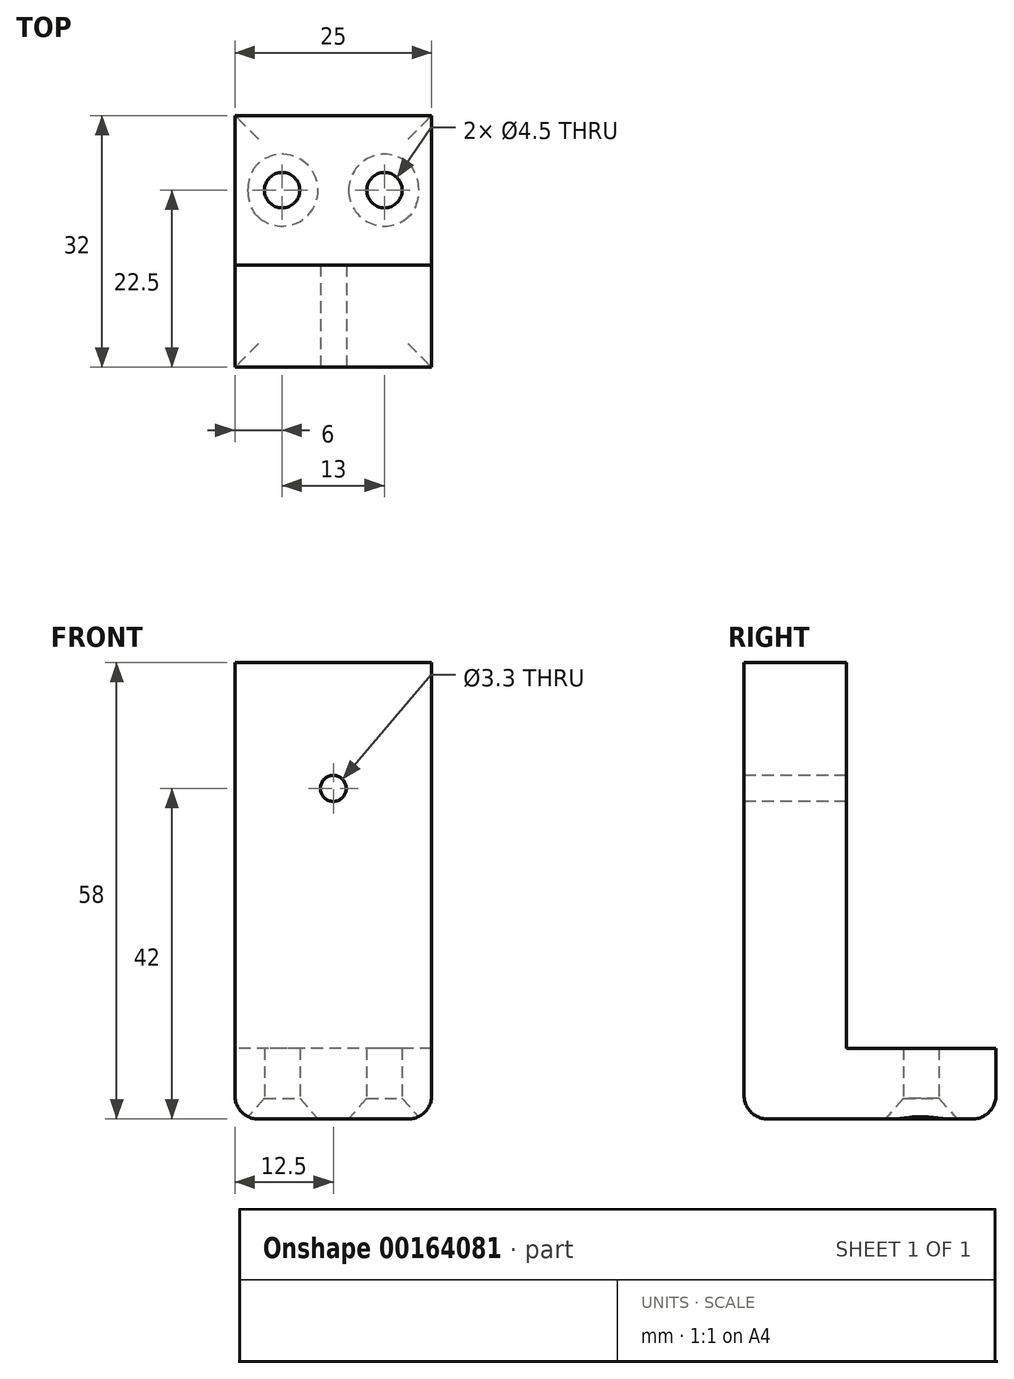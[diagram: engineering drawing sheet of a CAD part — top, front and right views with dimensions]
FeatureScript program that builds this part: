
annotation { "Feature Type Name" : "Feature", "Feature Type Description" : "" }
export const myFeature = defineFeature(function(context is Context, id is Id, definition is map)
    precondition{}
    {
        {
            var Q0;
            Q0=qCreatedBy(makeId("Right.planeOp"),FACE);
            var sketch = newSketch(context, id + "F0", { "sketchPlane" : qUnion([Q0])});
            skLineSegment(sketch, "E0", {"start": v(19, -58) * mm, "end": v(-13, -58) * mm});
            skLineSegment(sketch, "E1", {"start": v(-13, -58) * mm, "end": v(-13, 0) * mm});
            skLineSegment(sketch, "E2", {"start": v(-13, 0) * mm, "end": v(0, 0) * mm});
            skLineSegment(sketch, "E3", {"start": v(0, 0) * mm, "end": v(0, -49) * mm});
            skLineSegment(sketch, "E4", {"start": v(19, -58) * mm, "end": v(19, -49) * mm});
            skLineSegment(sketch, "E5", {"start": v(0, -49) * mm, "end": v(19, -49) * mm});
            skSolve(sketch);
        }
        {
            var Q0;
            Q0=makeQuery(id+"F0.imprint","IMPRINT",FACE,{"disambiguationData":[TD([[makeQuery(id+"F0.imprint","IMPRINT",EDGE,{"derivedFrom":sQuery(id+"F0.wireOp",EDGE,"E0")}),-1.0]])]});
            extrude(context, id + "F1", {"entities" : qUnion([Q0]), "depth" : 25 * mm});
        }
        {
            var Q0;
            Q0=makeQuery(id+"F1.opExtrude","SWEPT_FACE",FACE,{"disambiguationData":[OSD([sQuery(id+"F0.wireOp",EDGE,"E0")])]});
            var sketch = newSketch(context, id + "F2", { "sketchPlane" : qUnion([Q0])});
            skLineSegment(sketch, "E6.0.0", {"start": v(0, -19) * mm, "end": v(0, 0) * mm});
            skLineSegment(sketch, "E6.0.1", {"start": v(0, 0) * mm, "end": v(25, 0) * mm});
            skLineSegment(sketch, "E6.0.2", {"start": v(25, 0) * mm, "end": v(25, -19) * mm});
            skLineSegment(sketch, "E6.0.3", {"start": v(25, -19) * mm, "end": v(0, -19) * mm});
            skPoint(sketch, "E7", {"position": v(19, -9.5) * mm});
            skPoint(sketch, "E7.positionSnap0", {"position": v(25, -9.5) * mm});
            skPoint(sketch, "E8", {"position": v(6, -9.5) * mm});
            skSolve(sketch);
        }
        {
            var Q0;
            Q0=sQuery(id+"F2.wireOp",VERTEX,"E8");
            var Q1;
            Q1=sQuery(id+"F2.wireOp",VERTEX,"E7");
            var Q2;
            Q2=makeQuery(id+"F1.opExtrude","SWEPT_BODY",BODY,{"disambiguationData":[OSD([sQuery(id+"F0.wireOp",EDGE,"E0"),sQuery(id+"F0.wireOp",EDGE,"E1"),sQuery(id+"F0.wireOp",EDGE,"E2"),sQuery(id+"F0.wireOp",EDGE,"E3"),sQuery(id+"F0.wireOp",EDGE,"E4"),sQuery(id+"F0.wireOp",EDGE,"E5")])]});
            hole(context, id + "F3", {"style" : HoleStyle.C_SINK, "endStyle" : HoleEndStyle.THROUGH, "standardTappedOrClearance" : lookupTablePath({ "standard" : "ANSI", "fit" : "Normal (ASME)", "size" : "#8", "type" : "Clearance" }), "standardBlindInLast" : lookupTablePath({ "fit" : "Free", "standard" : "ANSI", "size" : "#8", "type" : "Clearance" }), "holeDiameter" : 4.5 * mm, "cSinkDiameter" : 9.12 * mm, "cSinkAngle" : 82 * degree, "locations" : qUnion([Q0, Q1]), "scope" : qUnion([Q2]), "isTappedThrough" : true});
        }
        {
            var Q0;
            Q0=makeQuery(id+"F1.opExtrude","SWEPT_FACE",FACE,{"disambiguationData":[OSD([sQuery(id+"F0.wireOp",EDGE,"E1")])]});
            var sketch = newSketch(context, id + "F4", { "sketchPlane" : qUnion([Q0])});
            skPoint(sketch, "E9", {"position": v(12.5, -16) * mm});
            skPoint(sketch, "E9.positionSnap0", {"position": v(12.5, 0) * mm});
            skSolve(sketch);
        }
        {
            var Q0;
            Q0=sQuery(id+"F4.wireOp",VERTEX,"E9");
            var Q1;
            Q1=makeQuery(id+"F1.opExtrude","SWEPT_BODY",BODY,{"disambiguationData":[OSD([sQuery(id+"F0.wireOp",EDGE,"E0"),sQuery(id+"F0.wireOp",EDGE,"E1"),sQuery(id+"F0.wireOp",EDGE,"E2"),sQuery(id+"F0.wireOp",EDGE,"E3"),sQuery(id+"F0.wireOp",EDGE,"E4"),sQuery(id+"F0.wireOp",EDGE,"E5")])]});
            hole(context, id + "F5", {"style" : HoleStyle.SIMPLE, "endStyle" : HoleEndStyle.THROUGH, "holeDiameter" : 3.3 * mm, "locations" : qUnion([Q0]), "scope" : qUnion([Q1]), "isTappedThrough" : true});
        }
        {
            var Q0;
            Q0=makeQuery(id+"F1.opExtrude","SWEPT_EDGE",EDGE,{"disambiguationData":[OSD([sQuery(id+"F0.wireOp",EDGE,"E0"),sQuery(id+"F0.wireOp",EDGE,"E1")])]});
            var Q1;
            Q1=makeQuery(id+"F1.opExtrude","CAP_EDGE",EDGE,{"disambiguationData":[OSD([sQuery(id+"F0.wireOp",EDGE,"E0")])],"isStart":false});
            var Q2;
            Q2=makeQuery(id+"F1.opExtrude","CAP_EDGE",EDGE,{"disambiguationData":[OSD([sQuery(id+"F0.wireOp",EDGE,"E0")])],"isStart":true});
            var Q3;
            Q3=makeQuery(id+"F1.opExtrude","SWEPT_EDGE",EDGE,{"disambiguationData":[OSD([sQuery(id+"F0.wireOp",EDGE,"E0"),sQuery(id+"F0.wireOp",EDGE,"E4")])]});
            fillet(context, id + "F6", {"entities" : qUnion([Q0, Q1, Q2, Q3]), "radius" : 3 * mm, "tangentPropagation" : true, "allowEdgeOverflow" : false});
        }
    });
